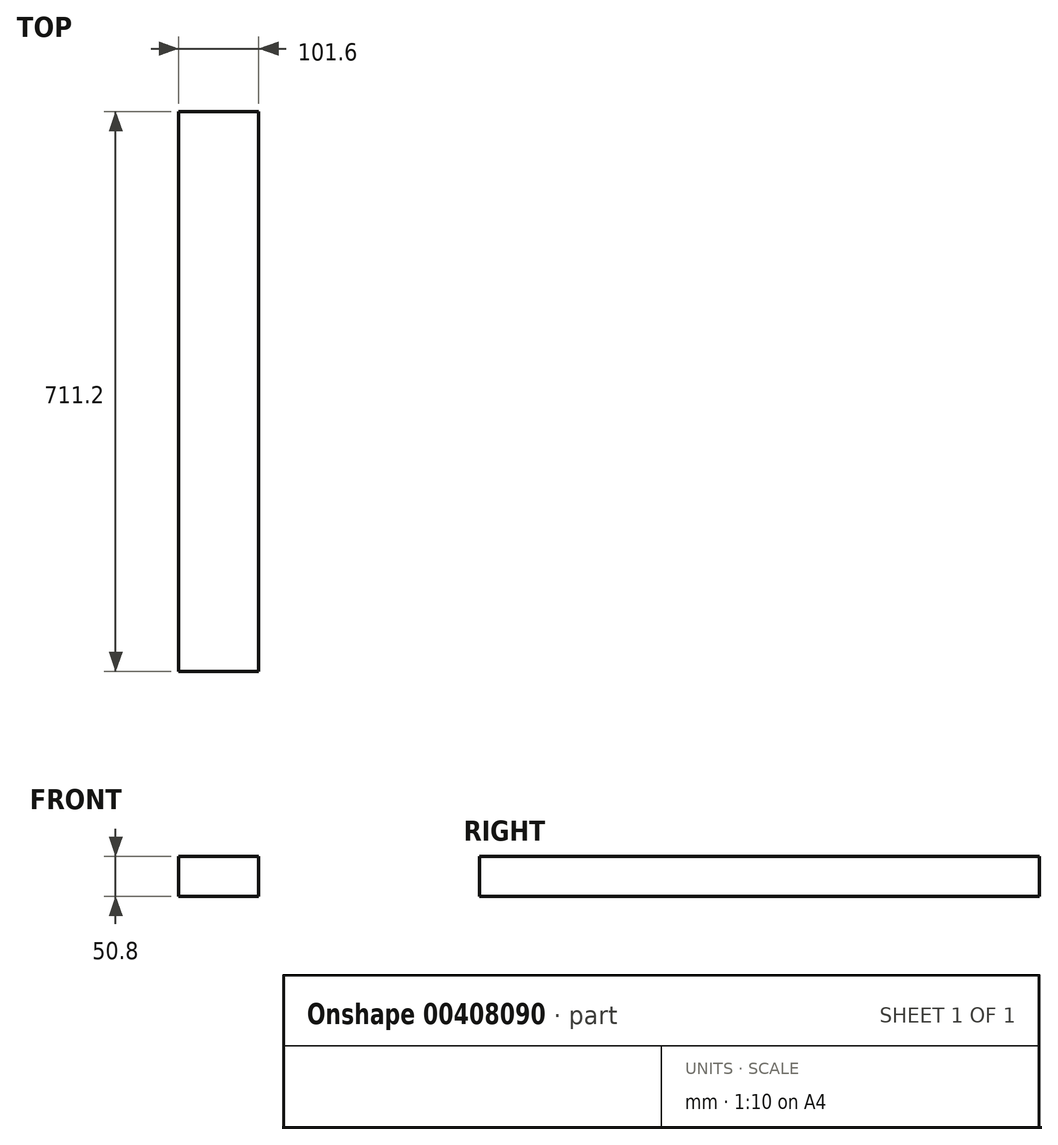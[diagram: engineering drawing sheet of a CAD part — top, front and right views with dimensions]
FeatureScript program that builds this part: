
annotation { "Feature Type Name" : "Feature", "Feature Type Description" : "" }
export const myFeature = defineFeature(function(context is Context, id is Id, definition is map)
    precondition{}
    {
        {
            var Q0;
            Q0=qCreatedBy(makeId("Top.planeOp"),FACE);
            var sketch = newSketch(context, id + "F0", { "sketchPlane" : qUnion([Q0])});
            skLineSegment(sketch, "E0.bottom", {"start": v(50.8, 355.6) * mm, "end": v(-50.8, 355.6) * mm});
            skLineSegment(sketch, "E0.top", {"start": v(50.8, -355.6) * mm, "end": v(-50.8, -355.6) * mm});
            skLineSegment(sketch, "E0.left", {"start": v(50.8, 355.6) * mm, "end": v(50.8, -355.6) * mm});
            skLineSegment(sketch, "E0.right", {"start": v(-50.8, 355.6) * mm, "end": v(-50.8, -355.6) * mm});
            skPoint(sketch, "E0.middle", {"position": v(0, 0) * mm});
            skSolve(sketch);
        }
        {
            var Q0;
            Q0 = qSketchRegion(id + "F0", true);
            extrude(context, id + "F1", {"entities" : qUnion([Q0]), "depth" : 50.8 * mm});
        }
    });
